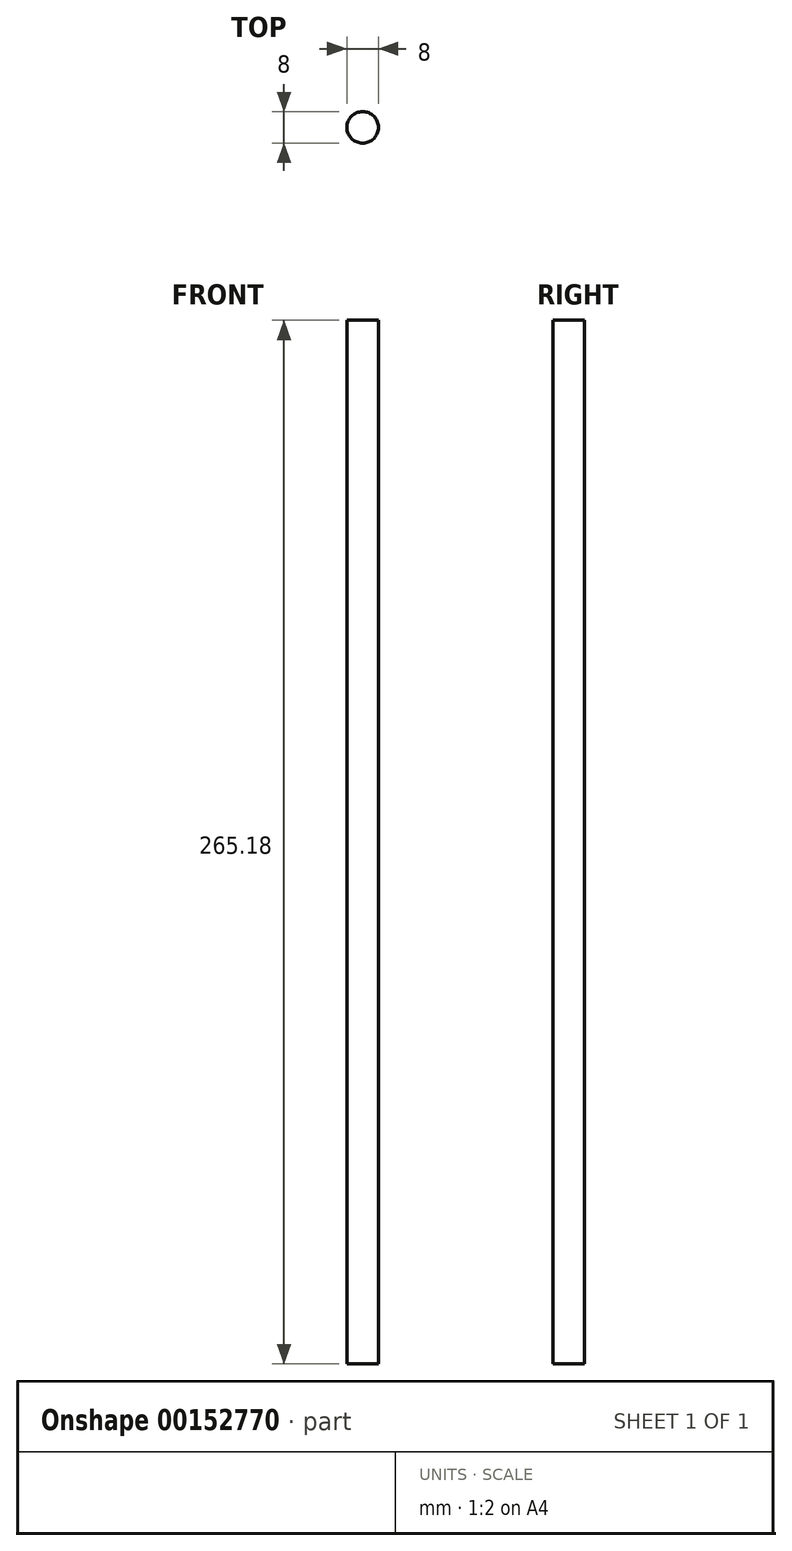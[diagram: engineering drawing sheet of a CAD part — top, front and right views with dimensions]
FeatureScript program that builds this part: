
annotation { "Feature Type Name" : "Feature", "Feature Type Description" : "" }
export const myFeature = defineFeature(function(context is Context, id is Id, definition is map)
    precondition{}
    {
        {
            var Q0;
            Q0=qCreatedBy(makeId("Top.planeOp"),FACE);
            var sketch = newSketch(context, id + "F0", { "sketchPlane" : qUnion([Q0])});
            skCircle(sketch, "E0", {"center": v(0, 0) * mm, "radius": 4 * mm});
            skSolve(sketch);
        }
        {
            var Q0;
            Q0=qSketchRegion(id+"F0",true);
            extrude(context, id + "F1", {"entities" : qUnion([Q0]), "depth" : 265.18 * mm});
        }
    });
